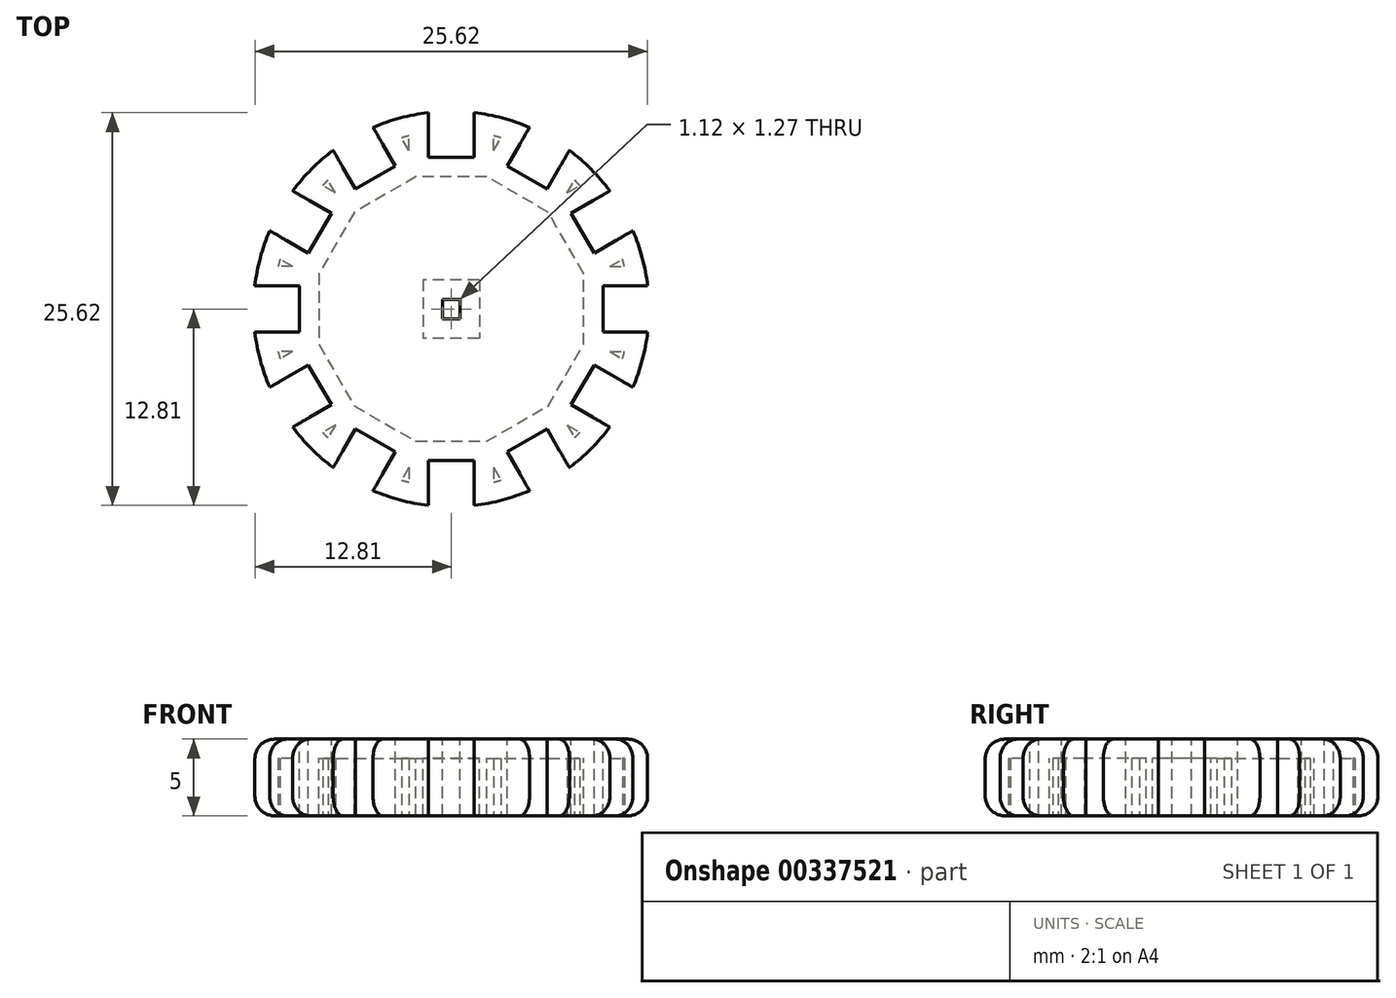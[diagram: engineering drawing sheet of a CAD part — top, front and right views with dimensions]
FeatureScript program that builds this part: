
annotation { "Feature Type Name" : "Feature", "Feature Type Description" : "" }
export const myFeature = defineFeature(function(context is Context, id is Id, definition is map)
    precondition{}
    {
        {
            var Q0;
            Q0=qCreatedBy(makeId("Top.planeOp"),FACE);
            var sketch = newSketch(context, id + "F0", { "sketchPlane" : qUnion([Q0])});
            skCircle(sketch, "E0", {"center": v(0, 0) * mm, "radius": 12.9 * mm});
            skSolve(sketch);
        }
        {
            var Q0;
            Q0=makeQuery(id+"F0.imprint","IMPRINT",FACE,{"disambiguationData":[TD([[makeQuery(id+"F0.imprint","IMPRINT",EDGE,{"derivedFrom":sQuery(id+"F0.wireOp",EDGE,"E0")}),1.0]])]});
            extrude(context, id + "F1", {"entities" : qUnion([Q0]), "depth" : 5 * mm});
        }
        {
            var Q0;
            Q0=makeQuery(id+"F1.opExtrude","CAP_FACE",FACE,{"disambiguationData":[OSD([sQuery(id+"F0.wireOp",EDGE,"E0")])],"isStart":false});
            var sketch = newSketch(context, id + "F2", { "sketchPlane" : qUnion([Q0])});
            skLineSegment(sketch, "E1.bottom", {"start": v(0.56, 0.64) * mm, "end": v(-0.56, 0.64) * mm});
            skLineSegment(sketch, "E1.top", {"start": v(0.56, -0.64) * mm, "end": v(-0.56, -0.64) * mm});
            skLineSegment(sketch, "E1.left", {"start": v(0.56, 0.64) * mm, "end": v(0.56, -0.64) * mm});
            skLineSegment(sketch, "E1.right", {"start": v(-0.56, 0.64) * mm, "end": v(-0.56, -0.64) * mm});
            skPoint(sketch, "E1.middle", {"position": v(0, 0) * mm});
            skLineSegment(sketch, "E2.bottom", {"start": v(-9.9, 1.5) * mm, "end": v(-15.9, 1.5) * mm});
            skLineSegment(sketch, "E2.top", {"start": v(-9.9, -1.5) * mm, "end": v(-15.9, -1.5) * mm});
            skLineSegment(sketch, "E2.left", {"start": v(-9.9, 1.5) * mm, "end": v(-9.9, -1.5) * mm});
            skLineSegment(sketch, "E2.right", {"start": v(-15.9, 1.5) * mm, "end": v(-15.9, -1.5) * mm});
            skPoint(sketch, "E2.middle", {"position": v(-12.9, 0) * mm});
            skLineSegment(sketch, "E3.1.0", {"start": v(-14.52, -6.65) * mm, "end": v(-13.02, -9.25) * mm});
            skPoint(sketch, "E3.1.1", {"position": v(-11.17, -6.45) * mm});
            skLineSegment(sketch, "E3.1.2", {"start": v(-9.32, -3.65) * mm, "end": v(-14.52, -6.65) * mm});
            skLineSegment(sketch, "E3.1.3", {"start": v(-7.82, -6.25) * mm, "end": v(-13.02, -9.25) * mm});
            skLineSegment(sketch, "E3.1.4", {"start": v(-9.32, -3.65) * mm, "end": v(-7.82, -6.25) * mm});
            skLineSegment(sketch, "E3.2.0", {"start": v(-9.25, -13.02) * mm, "end": v(-6.65, -14.52) * mm});
            skPoint(sketch, "E3.2.1", {"position": v(-6.45, -11.17) * mm});
            skLineSegment(sketch, "E3.2.2", {"start": v(-6.25, -7.82) * mm, "end": v(-9.25, -13.02) * mm});
            skLineSegment(sketch, "E3.2.3", {"start": v(-3.65, -9.32) * mm, "end": v(-6.65, -14.52) * mm});
            skLineSegment(sketch, "E3.2.4", {"start": v(-6.25, -7.82) * mm, "end": v(-3.65, -9.32) * mm});
            skLineSegment(sketch, "E3.3.0", {"start": v(-1.5, -15.9) * mm, "end": v(1.5, -15.9) * mm});
            skPoint(sketch, "E3.3.1", {"position": v(0, -12.9) * mm});
            skLineSegment(sketch, "E3.3.2", {"start": v(-1.5, -9.9) * mm, "end": v(-1.5, -15.9) * mm});
            skLineSegment(sketch, "E3.3.3", {"start": v(1.5, -9.9) * mm, "end": v(1.5, -15.9) * mm});
            skLineSegment(sketch, "E3.3.4", {"start": v(-1.5, -9.9) * mm, "end": v(1.5, -9.9) * mm});
            skLineSegment(sketch, "E3.4.0", {"start": v(6.65, -14.52) * mm, "end": v(9.25, -13.02) * mm});
            skPoint(sketch, "E3.4.1", {"position": v(6.45, -11.17) * mm});
            skLineSegment(sketch, "E3.4.2", {"start": v(3.65, -9.32) * mm, "end": v(6.65, -14.52) * mm});
            skLineSegment(sketch, "E3.4.3", {"start": v(6.25, -7.82) * mm, "end": v(9.25, -13.02) * mm});
            skLineSegment(sketch, "E3.4.4", {"start": v(3.65, -9.32) * mm, "end": v(6.25, -7.82) * mm});
            skLineSegment(sketch, "E3.5.0", {"start": v(13.02, -9.25) * mm, "end": v(14.52, -6.65) * mm});
            skPoint(sketch, "E3.5.1", {"position": v(11.17, -6.45) * mm});
            skLineSegment(sketch, "E3.5.2", {"start": v(7.82, -6.25) * mm, "end": v(13.02, -9.25) * mm});
            skLineSegment(sketch, "E3.5.3", {"start": v(9.32, -3.65) * mm, "end": v(14.52, -6.65) * mm});
            skLineSegment(sketch, "E3.5.4", {"start": v(7.82, -6.25) * mm, "end": v(9.32, -3.65) * mm});
            skLineSegment(sketch, "E3.6.0", {"start": v(15.9, -1.5) * mm, "end": v(15.9, 1.5) * mm});
            skPoint(sketch, "E3.6.1", {"position": v(12.9, 0) * mm});
            skLineSegment(sketch, "E3.6.2", {"start": v(9.9, -1.5) * mm, "end": v(15.9, -1.5) * mm});
            skLineSegment(sketch, "E3.6.3", {"start": v(9.9, 1.5) * mm, "end": v(15.9, 1.5) * mm});
            skLineSegment(sketch, "E3.6.4", {"start": v(9.9, -1.5) * mm, "end": v(9.9, 1.5) * mm});
            skLineSegment(sketch, "E3.7.0", {"start": v(14.52, 6.65) * mm, "end": v(13.02, 9.25) * mm});
            skPoint(sketch, "E3.7.1", {"position": v(11.17, 6.45) * mm});
            skLineSegment(sketch, "E3.7.2", {"start": v(9.32, 3.65) * mm, "end": v(14.52, 6.65) * mm});
            skLineSegment(sketch, "E3.7.3", {"start": v(7.82, 6.25) * mm, "end": v(13.02, 9.25) * mm});
            skLineSegment(sketch, "E3.7.4", {"start": v(9.32, 3.65) * mm, "end": v(7.82, 6.25) * mm});
            skLineSegment(sketch, "E3.8.0", {"start": v(9.25, 13.02) * mm, "end": v(6.65, 14.52) * mm});
            skPoint(sketch, "E3.8.1", {"position": v(6.45, 11.17) * mm});
            skLineSegment(sketch, "E3.8.2", {"start": v(6.25, 7.82) * mm, "end": v(9.25, 13.02) * mm});
            skLineSegment(sketch, "E3.8.3", {"start": v(3.65, 9.32) * mm, "end": v(6.65, 14.52) * mm});
            skLineSegment(sketch, "E3.8.4", {"start": v(6.25, 7.82) * mm, "end": v(3.65, 9.32) * mm});
            skLineSegment(sketch, "E3.9.0", {"start": v(1.5, 15.9) * mm, "end": v(-1.5, 15.9) * mm});
            skPoint(sketch, "E3.9.1", {"position": v(0, 12.9) * mm});
            skLineSegment(sketch, "E3.9.2", {"start": v(1.5, 9.9) * mm, "end": v(1.5, 15.9) * mm});
            skLineSegment(sketch, "E3.9.3", {"start": v(-1.5, 9.9) * mm, "end": v(-1.5, 15.9) * mm});
            skLineSegment(sketch, "E3.9.4", {"start": v(1.5, 9.9) * mm, "end": v(-1.5, 9.9) * mm});
            skLineSegment(sketch, "E3.10.0", {"start": v(-6.65, 14.52) * mm, "end": v(-9.25, 13.02) * mm});
            skPoint(sketch, "E3.10.1", {"position": v(-6.45, 11.17) * mm});
            skLineSegment(sketch, "E3.10.2", {"start": v(-3.65, 9.32) * mm, "end": v(-6.65, 14.52) * mm});
            skLineSegment(sketch, "E3.10.3", {"start": v(-6.25, 7.82) * mm, "end": v(-9.25, 13.02) * mm});
            skLineSegment(sketch, "E3.10.4", {"start": v(-3.65, 9.32) * mm, "end": v(-6.25, 7.82) * mm});
            skLineSegment(sketch, "E3.11.0", {"start": v(-13.02, 9.25) * mm, "end": v(-14.52, 6.65) * mm});
            skPoint(sketch, "E3.11.1", {"position": v(-11.17, 6.45) * mm});
            skLineSegment(sketch, "E3.11.2", {"start": v(-7.82, 6.25) * mm, "end": v(-13.02, 9.25) * mm});
            skLineSegment(sketch, "E3.11.3", {"start": v(-9.32, 3.65) * mm, "end": v(-14.52, 6.65) * mm});
            skLineSegment(sketch, "E3.11.4", {"start": v(-7.82, 6.25) * mm, "end": v(-9.32, 3.65) * mm});
            skSolve(sketch);
        }
        {
            var Q0;
            {var subQ0=sQuery(id+"F0.wireOp",EDGE,"E0");Q0=makeQuery(id+"F4.boolean.opBoolean","SPLIT",EDGE,{"disambiguationData":[TD([makeQuery(id+"F4.opExtrude","SWEPT_FACE",FACE,{"disambiguationData":[OSD([sQuery(id+"F2.wireOp",EDGE,"E3.4.3")])]})])],"derivedFrom":makeQuery(id+"F1.opExtrude","CAP_EDGE",EDGE,{"disambiguationData":[OSD([subQ0])],"isStart":true})});}
            var Q1;
            Q1=makeQuery(id+"F1.opExtrude","CAP_EDGE",EDGE,{"disambiguationData":[OSD([sQuery(id+"F0.wireOp",EDGE,"E0")])],"isStart":false});
            fillet(context, id + "F3", {"entities" : qUnion([Q0, Q1]), "radius" : 1.27 * mm, "tangentPropagation" : true, "allowEdgeOverflow" : false});
        }
        {
            var Q0;
            Q0 = qSketchRegion(id + "F2", true);
            extrude(context, id + "F4", {"entities" : qUnion([Q0]), "operationType" : NewBodyOperationType.REMOVE, "endBound" : BoundingType.THROUGH_ALL, "oppositeDirection" : true, "depth" : 25.4 * mm});
        }
        {
            var Q0;
            Q0=makeQuery(id+"F1.opExtrude","CAP_FACE",FACE,{"disambiguationData":[OSD([sQuery(id+"F0.wireOp",EDGE,"E0")])],"isStart":true});
            shell(context, id + "F5", {"entities" : qUnion([Q0]), "thickness" : 1.27 * mm});
        }
    });
